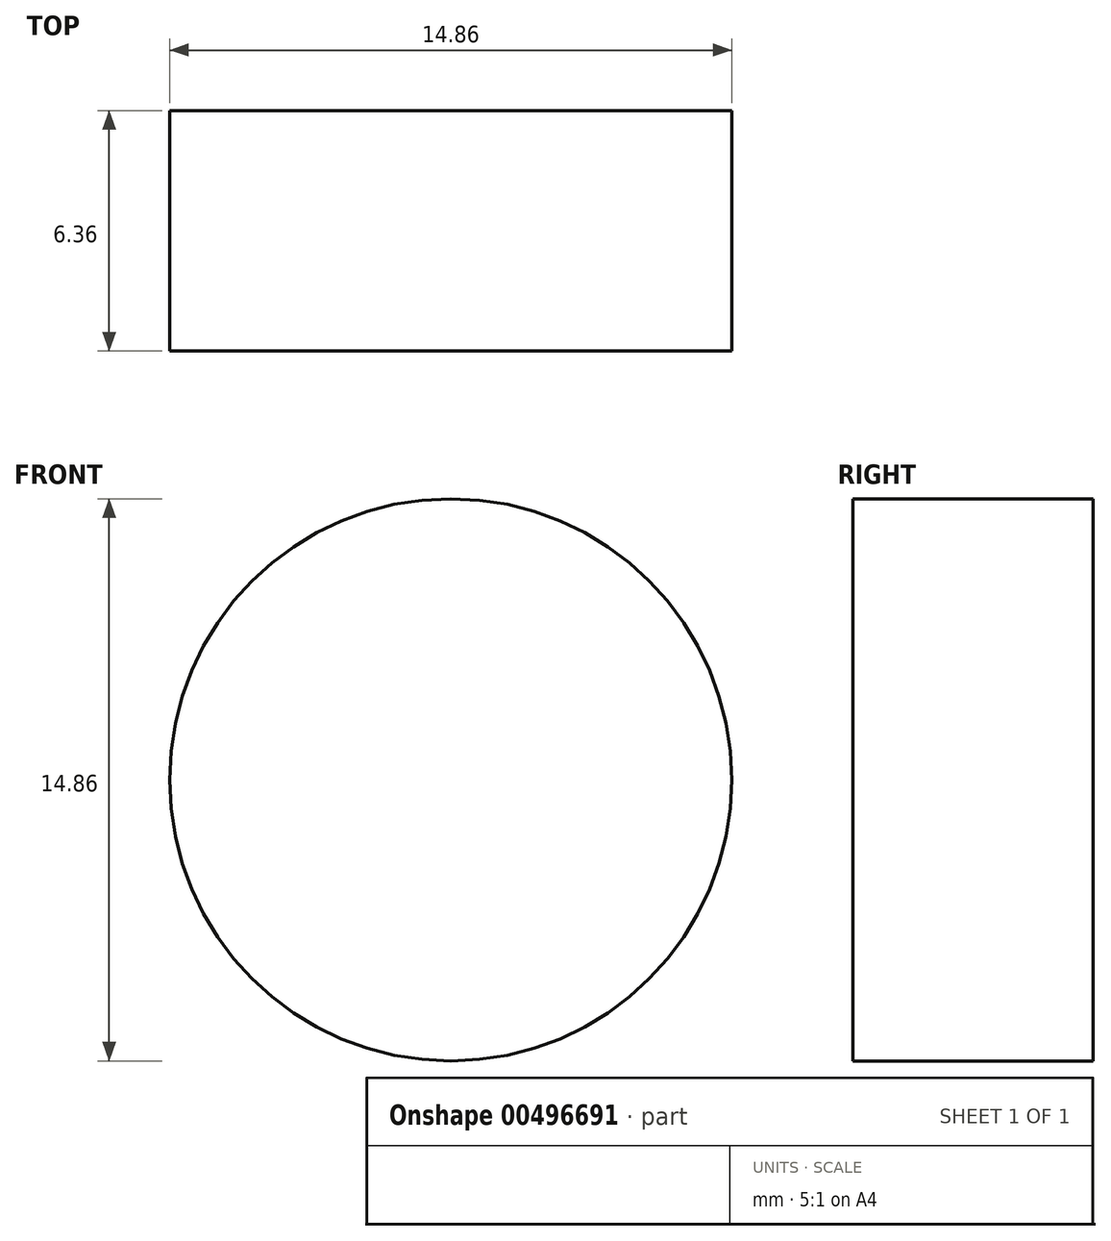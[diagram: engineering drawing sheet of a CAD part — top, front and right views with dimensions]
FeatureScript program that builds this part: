
annotation { "Feature Type Name" : "Feature", "Feature Type Description" : "" }
export const myFeature = defineFeature(function(context is Context, id is Id, definition is map)
    precondition{}
    {
        {
            var Q0;
            Q0=qCreatedBy(makeId("Front.planeOp"),FACE);
            var sketch = newSketch(context, id + "F0", { "sketchPlane" : qUnion([Q0])});
            skCircle(sketch, "E0", {"center": v(0, 0) * mm, "radius": 7.43 * mm});
            skSolve(sketch);
        }
        {
            var Q0;
            Q0=makeQuery(id+"F0.imprint","IMPRINT",FACE,{"disambiguationData":[TD([[makeQuery(id+"F0.imprint","IMPRINT",EDGE,{"derivedFrom":sQuery(id+"F0.wireOp",EDGE,"E0")}),1.0]])]});
            extrude(context, id + "F1", {"entities" : qUnion([Q0]), "endBound" : BoundingType.SYMMETRIC, "depth" : 6.35 * mm});
        }
    });
